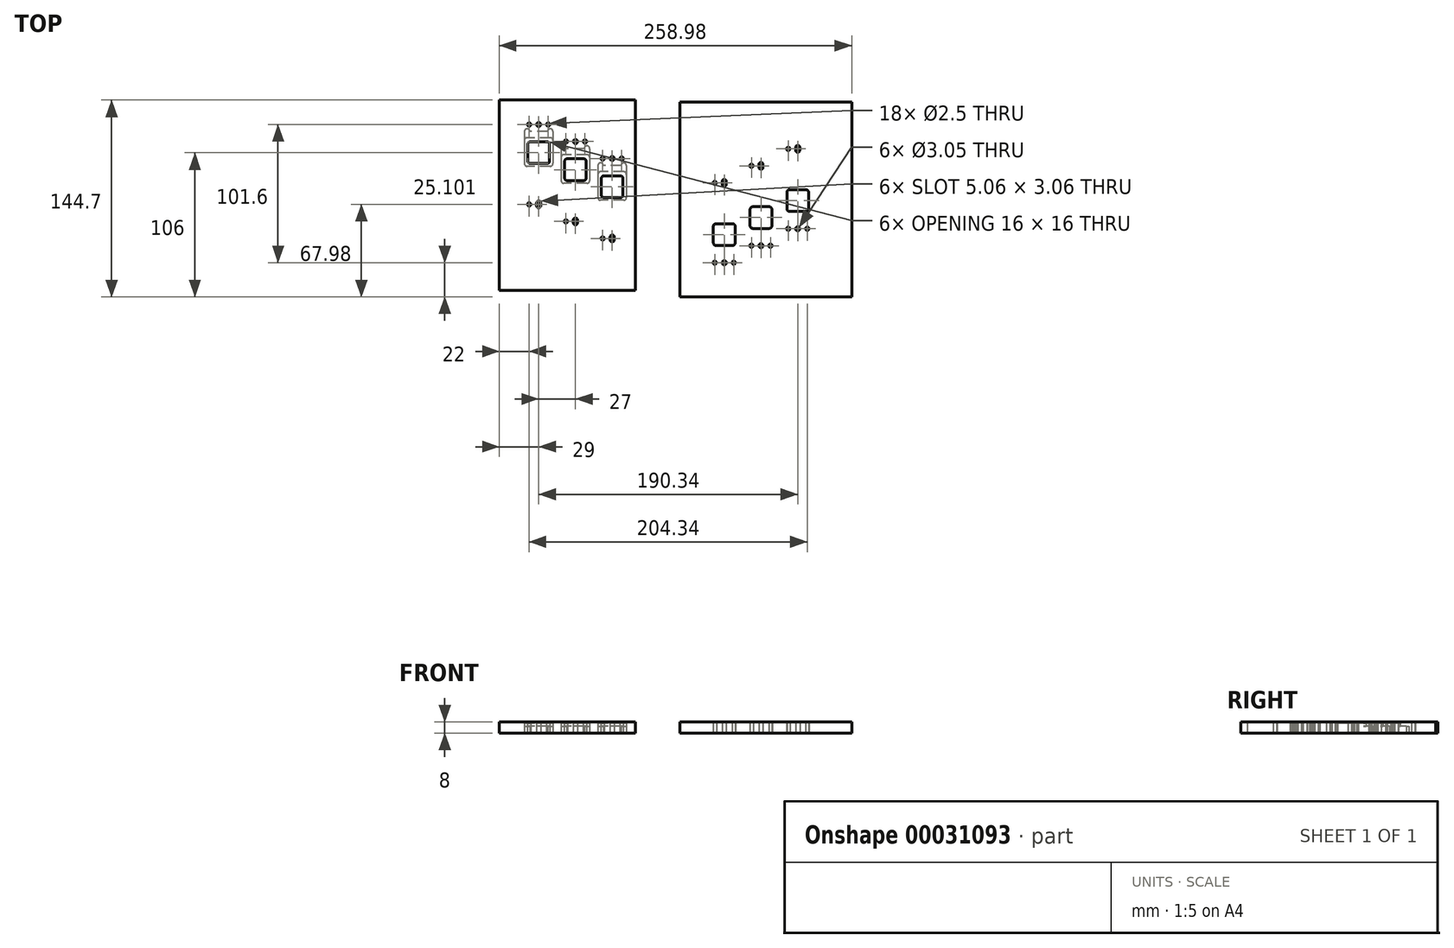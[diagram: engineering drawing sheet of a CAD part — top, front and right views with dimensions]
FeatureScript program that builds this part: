
annotation { "Feature Type Name" : "Feature", "Feature Type Description" : "" }
export const myFeature = defineFeature(function(context is Context, id is Id, definition is map)
    precondition{}
    {
        {
            var Q0;
            Q0=qCreatedBy(makeId("Top.planeOp"),FACE);
            var sketch = newSketch(context, id + "F0", { "sketchPlane" : qUnion([Q0])});
            skLineSegment(sketch, "E0.bottom", {"start": v(-50, 70) * mm, "end": v(50, 70) * mm});
            skLineSegment(sketch, "E0.top", {"start": v(-50, -70) * mm, "end": v(50, -70) * mm});
            skLineSegment(sketch, "E0.left", {"start": v(-50, 70) * mm, "end": v(-50, -70) * mm});
            skLineSegment(sketch, "E0.right", {"start": v(50, 70) * mm, "end": v(50, -70) * mm});
            skLineSegment(sketch, "E1", {"start": v(-50, -70) * mm, "end": v(50, 70) * mm, "construction": true});
            skSolve(sketch);
        }
        {
            var Q0;
            Q0=qSketchRegion(id+"F0",true);
            extrude(context, id + "F1", {"entities" : qUnion([Q0]), "depth" : 8 * mm});
        }
        {
            var Q0;
            Q0=makeQuery(id+"F1.opExtrude","CAP_FACE",FACE,{"disambiguationData":[OSD([sQuery(id+"F0.wireOp",EDGE,"E0.bottom"),sQuery(id+"F0.wireOp",EDGE,"E0.top"),sQuery(id+"F0.wireOp",EDGE,"E0.left"),sQuery(id+"F0.wireOp",EDGE,"E0.right")])],"isStart":true});
            var sketch = newSketch(context, id + "F2", { "sketchPlane" : qUnion([Q0])});
            skLineSegment(sketch, "E2", {"start": v(-21, -52) * mm, "end": v(-21, 6.72) * mm, "construction": true});
            skLineSegment(sketch, "E3", {"start": v(6, -39.5) * mm, "end": v(6, 19.22) * mm, "construction": true});
            skLineSegment(sketch, "E4", {"start": v(33, -27) * mm, "end": v(33, 31.72) * mm, "construction": true});
            skLineSegment(sketch, "E5", {"start": v(-14, -52) * mm, "end": v(-28, -52) * mm, "construction": true});
            skLineSegment(sketch, "E6", {"start": v(13, -39.5) * mm, "end": v(-1, -39.5) * mm, "construction": true});
            skLineSegment(sketch, "E7", {"start": v(40, -27) * mm, "end": v(26, -27) * mm, "construction": true});
            skLineSegment(sketch, "E8", {"start": v(-21, 6.72) * mm, "end": v(-28, 6.72) * mm, "construction": true});
            skLineSegment(sketch, "E9", {"start": v(6, 19.22) * mm, "end": v(-1, 19.22) * mm, "construction": true});
            skLineSegment(sketch, "E10", {"start": v(33, 31.72) * mm, "end": v(26, 31.72) * mm, "construction": true});
            skCircle(sketch, "E11", {"center": v(-28, -52) * mm, "radius": 1.25 * mm});
            skCircle(sketch, "E12", {"center": v(-14, -52) * mm, "radius": 1.25 * mm});
            skCircle(sketch, "E13", {"center": v(-28, 6.72) * mm, "radius": 1.25 * mm});
            skCircle(sketch, "E14", {"center": v(-1, -39.5) * mm, "radius": 1.25 * mm});
            skCircle(sketch, "E15", {"center": v(13, -39.5) * mm, "radius": 1.25 * mm});
            skCircle(sketch, "E16", {"center": v(-1, 19.22) * mm, "radius": 1.25 * mm});
            skCircle(sketch, "E17", {"center": v(26, 31.72) * mm, "radius": 1.25 * mm});
            skCircle(sketch, "E18", {"center": v(26, -27) * mm, "radius": 1.25 * mm});
            skCircle(sketch, "E19", {"center": v(40, -27) * mm, "radius": 1.25 * mm});
            skLineSegment(sketch, "E20", {"start": v(-21, 5.72) * mm, "end": v(-21, 7.72) * mm});
            skArc(sketch, "E21.0.startCap", {"start": v(-19.47, 5.72) * mm, "mid": v(-21, 4.2) * mm, "end": v(-22.53, 5.72) * mm});
            skArc(sketch, "E21.0.endCap", {"start": v(-22.53, 7.72) * mm, "mid": v(-21, 9.25) * mm, "end": v(-19.47, 7.72) * mm});
            skLineSegment(sketch, "E21.0.left", {"start": v(-22.53, 5.72) * mm, "end": v(-22.53, 7.72) * mm});
            skLineSegment(sketch, "E21.0.right", {"start": v(-19.47, 5.72) * mm, "end": v(-19.47, 7.72) * mm});
            skArc(sketch, "E22.0.startCap", {"start": v(7.53, 18.22) * mm, "mid": v(6, 16.7) * mm, "end": v(4.47, 18.22) * mm});
            skLineSegment(sketch, "E22.0.left", {"start": v(4.47, 18.22) * mm, "end": v(4.47, 20.22) * mm});
            skLineSegment(sketch, "E23", {"start": v(6, 18.22) * mm, "end": v(6, 20.22) * mm});
            skLineSegment(sketch, "E22.0.right", {"start": v(7.53, 18.22) * mm, "end": v(7.53, 20.22) * mm});
            skArc(sketch, "E22.0.endCap", {"start": v(4.47, 20.22) * mm, "mid": v(6, 21.75) * mm, "end": v(7.53, 20.22) * mm});
            skArc(sketch, "E24.0.startCap", {"start": v(34.53, 30.72) * mm, "mid": v(33, 29.2) * mm, "end": v(31.47, 30.72) * mm});
            skLineSegment(sketch, "E24.0.left", {"start": v(31.47, 30.72) * mm, "end": v(31.47, 32.72) * mm});
            skLineSegment(sketch, "E25", {"start": v(33, 30.72) * mm, "end": v(33, 32.72) * mm});
            skLineSegment(sketch, "E24.0.right", {"start": v(34.53, 30.72) * mm, "end": v(34.53, 32.72) * mm});
            skArc(sketch, "E24.0.endCap", {"start": v(31.47, 32.72) * mm, "mid": v(33, 34.25) * mm, "end": v(34.53, 32.72) * mm});
            skCircle(sketch, "E26", {"center": v(33, -27) * mm, "radius": 1.52 * mm});
            skCircle(sketch, "E27", {"center": v(6, -39.5) * mm, "radius": 1.52 * mm});
            skCircle(sketch, "E28", {"center": v(-21, -52) * mm, "radius": 1.52 * mm});
            skSolve(sketch);
        }
        {
            var Q0;
            Q0=qSketchRegion(id+"F2",true);
            var Q1;
            Q1=makeQuery(id+"F1.opExtrude","CAP_FACE",FACE,{"disambiguationData":[OSD([sQuery(id+"F0.wireOp",EDGE,"E0.bottom"),sQuery(id+"F0.wireOp",EDGE,"E0.top"),sQuery(id+"F0.wireOp",EDGE,"E0.left"),sQuery(id+"F0.wireOp",EDGE,"E0.right")])],"isStart":false});
            extrude(context, id + "F3", {"entities" : qUnion([Q0]), "operationType" : NewBodyOperationType.REMOVE, "endBound" : BoundingType.UP_TO_SURFACE, "oppositeDirection" : true, "endBoundEntityFace" : qUnion([Q1]), "depth" : 25 * mm});
        }
        {
            var Q0;
            Q0=makeQuery(id+"F1.opExtrude","CAP_FACE",FACE,{"disambiguationData":[OSD([sQuery(id+"F0.wireOp",EDGE,"E0.bottom"),sQuery(id+"F0.wireOp",EDGE,"E0.top"),sQuery(id+"F0.wireOp",EDGE,"E0.left"),sQuery(id+"F0.wireOp",EDGE,"E0.right")])],"isStart":true});
            var sketch = newSketch(context, id + "F4", { "sketchPlane" : qUnion([Q0])});
            skCircle(sketch, "E29", {"center": v(40, -27) * mm, "radius": 1.5 * mm});
            skCircle(sketch, "E30", {"center": v(26, -27) * mm, "radius": 1.5 * mm});
            skCircle(sketch, "E31", {"center": v(13, -39.5) * mm, "radius": 1.5 * mm});
            skCircle(sketch, "E32", {"center": v(-1, -39.5) * mm, "radius": 1.5 * mm});
            skCircle(sketch, "E33", {"center": v(-14, -52) * mm, "radius": 1.5 * mm});
            skCircle(sketch, "E34", {"center": v(-28, -52) * mm, "radius": 1.5 * mm});
            skCircle(sketch, "E35", {"center": v(-1, 19.22) * mm, "radius": 1.5 * mm});
            skCircle(sketch, "E36", {"center": v(-28, 6.72) * mm, "radius": 1.5 * mm});
            skCircle(sketch, "E37", {"center": v(26, 31.72) * mm, "radius": 1.5 * mm});
            skSolve(sketch);
        }
        {
            var Q0;
            Q0=makeQuery(id+"F4.imprint","IMPRINT",FACE,{"disambiguationData":[TD([[makeQuery(id+"F4.imprint","IMPRINT",EDGE,{"derivedFrom":sQuery(id+"F4.wireOp",EDGE,"E29")}),-1.0]])]});
            var sketch = newSketch(context, id + "F5", { "sketchPlane" : qUnion([Q0])});
            skLineSegment(sketch, "E38.bottom", {"start": v(39.5, -21.8) * mm, "end": v(26.5, -21.8) * mm});
            skLineSegment(sketch, "E38.top", {"start": v(41.5, 3.7) * mm, "end": v(24.5, 3.7) * mm});
            skLineSegment(sketch, "E38.left", {"start": v(43.5, -21.8) * mm, "end": v(43.5, 1.7) * mm});
            skLineSegment(sketch, "E38.right", {"start": v(22.5, -21.8) * mm, "end": v(22.5, 1.7) * mm});
            skLineSegment(sketch, "E39", {"start": v(33, -21.8) * mm, "end": v(33, -27) * mm, "construction": true});
            skArc(sketch, "E40", {"start": v(39.5, -21.8) * mm, "mid": v(41.5, -23.8) * mm, "end": v(43.5, -21.8) * mm});
            skArc(sketch, "E41", {"start": v(22.5, -21.8) * mm, "mid": v(24.5, -23.8) * mm, "end": v(26.5, -21.8) * mm});
            skPoint(sketch, "E42.visualSharp", {"position": v(43.5, 3.7) * mm});
            skArc(sketch, "E42.filletArc", {"start": v(43.5, 1.7) * mm, "mid": v(42.91, 3.11) * mm, "end": v(41.5, 3.7) * mm});
            skPoint(sketch, "E43.visualSharp", {"position": v(22.5, 3.7) * mm});
            skArc(sketch, "E43.filletArc", {"start": v(24.5, 3.7) * mm, "mid": v(23.09, 3.11) * mm, "end": v(22.5, 1.7) * mm});
            skLineSegment(sketch, "E44.top", {"start": v(14.5, -8.8) * mm, "end": v(-2.5, -8.8) * mm});
            skLineSegment(sketch, "E44.bottom", {"start": v(12.5, -34.3) * mm, "end": v(-0.5, -34.3) * mm});
            skLineSegment(sketch, "E44.right", {"start": v(-4.5, -34.3) * mm, "end": v(-4.5, -10.8) * mm});
            skArc(sketch, "E45", {"start": v(12.5, -34.3) * mm, "mid": v(14.5, -36.3) * mm, "end": v(16.5, -34.3) * mm});
            skLineSegment(sketch, "E44.left", {"start": v(16.5, -34.3) * mm, "end": v(16.5, -10.8) * mm});
            skArc(sketch, "E46", {"start": v(-4.5, -34.3) * mm, "mid": v(-2.5, -36.3) * mm, "end": v(-0.5, -34.3) * mm});
            skPoint(sketch, "E47.visualSharp", {"position": v(16.5, -8.8) * mm});
            skPoint(sketch, "E48.visualSharp", {"position": v(-4.5, -8.8) * mm});
            skLineSegment(sketch, "E49", {"start": v(6, -34.3) * mm, "end": v(6, -39.5) * mm, "construction": true});
            skArc(sketch, "E48.filletArc", {"start": v(-2.5, -8.8) * mm, "mid": v(-3.91, -9.39) * mm, "end": v(-4.5, -10.8) * mm});
            skArc(sketch, "E47.filletArc", {"start": v(16.5, -10.8) * mm, "mid": v(15.91, -9.39) * mm, "end": v(14.5, -8.8) * mm});
            skLineSegment(sketch, "E50.top", {"start": v(-12.5, -21.3) * mm, "end": v(-29.5, -21.3) * mm});
            skLineSegment(sketch, "E50.bottom", {"start": v(-14.5, -46.8) * mm, "end": v(-27.5, -46.8) * mm});
            skLineSegment(sketch, "E50.right", {"start": v(-31.5, -46.8) * mm, "end": v(-31.5, -23.3) * mm});
            skArc(sketch, "E51", {"start": v(-14.5, -46.8) * mm, "mid": v(-12.5, -48.8) * mm, "end": v(-10.5, -46.8) * mm});
            skLineSegment(sketch, "E50.left", {"start": v(-10.5, -46.8) * mm, "end": v(-10.5, -23.3) * mm});
            skArc(sketch, "E52", {"start": v(-31.5, -46.8) * mm, "mid": v(-29.5, -48.8) * mm, "end": v(-27.5, -46.8) * mm});
            skPoint(sketch, "E53.visualSharp", {"position": v(-10.5, -21.3) * mm});
            skPoint(sketch, "E54.visualSharp", {"position": v(-31.5, -21.3) * mm});
            skLineSegment(sketch, "E55", {"start": v(-21, -46.8) * mm, "end": v(-21, -52) * mm, "construction": true});
            skArc(sketch, "E54.filletArc", {"start": v(-29.5, -21.3) * mm, "mid": v(-30.91, -21.89) * mm, "end": v(-31.5, -23.3) * mm});
            skArc(sketch, "E53.filletArc", {"start": v(-10.5, -23.3) * mm, "mid": v(-11.09, -21.89) * mm, "end": v(-12.5, -21.3) * mm});
            skSolve(sketch);
        }
        {
            var Q0;
            Q0=qSketchRegion(id+"F5",true);
            extrude(context, id + "F6", {"entities" : qUnion([Q0]), "operationType" : NewBodyOperationType.REMOVE, "oppositeDirection" : true, "depth" : 5 * mm});
        }
        {
            var Q0;
            Q0=makeQuery(id+"F4.imprint","IMPRINT",FACE,{"disambiguationData":[TD([[makeQuery(id+"F4.imprint","IMPRINT",EDGE,{"derivedFrom":sQuery(id+"F4.wireOp",EDGE,"E29")}),-1.0]])]});
            var sketch = newSketch(context, id + "F7", { "sketchPlane" : qUnion([Q0])});
            skLineSegment(sketch, "E56.bottom", {"start": v(41.5, -17.3) * mm, "end": v(24.5, -17.3) * mm});
            skLineSegment(sketch, "E56.top", {"start": v(41.5, 3.7) * mm, "end": v(24.5, 3.7) * mm});
            skLineSegment(sketch, "E56.left", {"start": v(43.5, -15.3) * mm, "end": v(43.5, 1.7) * mm});
            skLineSegment(sketch, "E56.right", {"start": v(22.5, -15.3) * mm, "end": v(22.5, 1.7) * mm});
            skLineSegment(sketch, "E57", {"start": v(33, -17.3) * mm, "end": v(33, -27) * mm, "construction": true});
            skPoint(sketch, "E58.visualSharp", {"position": v(43.5, -17.3) * mm});
            skArc(sketch, "E58.filletArc", {"start": v(41.5, -17.3) * mm, "mid": v(42.91, -16.71) * mm, "end": v(43.5, -15.3) * mm});
            skPoint(sketch, "E59.visualSharp", {"position": v(43.5, 3.7) * mm});
            skArc(sketch, "E59.filletArc", {"start": v(43.5, 1.7) * mm, "mid": v(42.91, 3.11) * mm, "end": v(41.5, 3.7) * mm});
            skPoint(sketch, "E60.visualSharp", {"position": v(22.5, 3.7) * mm});
            skArc(sketch, "E60.filletArc", {"start": v(24.5, 3.7) * mm, "mid": v(23.09, 3.11) * mm, "end": v(22.5, 1.7) * mm});
            skPoint(sketch, "E61.visualSharp", {"position": v(22.5, -17.3) * mm});
            skArc(sketch, "E61.filletArc", {"start": v(22.5, -15.3) * mm, "mid": v(23.09, -16.71) * mm, "end": v(24.5, -17.3) * mm});
            skPoint(sketch, "E62.visualSharp", {"position": v(-4.5, -8.8) * mm});
            skLineSegment(sketch, "E63.left", {"start": v(16.5, -27.8) * mm, "end": v(16.5, -10.8) * mm});
            skPoint(sketch, "E64.visualSharp", {"position": v(-4.5, -29.8) * mm});
            skLineSegment(sketch, "E63.bottom", {"start": v(14.5, -29.8) * mm, "end": v(-2.5, -29.8) * mm});
            skPoint(sketch, "E65.visualSharp", {"position": v(16.5, -8.8) * mm});
            skLineSegment(sketch, "E63.right", {"start": v(-4.5, -27.8) * mm, "end": v(-4.5, -10.8) * mm});
            skPoint(sketch, "E66.visualSharp", {"position": v(16.5, -29.8) * mm});
            skLineSegment(sketch, "E63.top", {"start": v(14.5, -8.8) * mm, "end": v(-2.5, -8.8) * mm});
            skArc(sketch, "E65.filletArc", {"start": v(16.5, -10.8) * mm, "mid": v(15.91, -9.39) * mm, "end": v(14.5, -8.8) * mm});
            skArc(sketch, "E66.filletArc", {"start": v(14.5, -29.8) * mm, "mid": v(15.91, -29.21) * mm, "end": v(16.5, -27.8) * mm});
            skArc(sketch, "E62.filletArc", {"start": v(-2.5, -8.8) * mm, "mid": v(-3.91, -9.39) * mm, "end": v(-4.5, -10.8) * mm});
            skArc(sketch, "E64.filletArc", {"start": v(-4.5, -27.8) * mm, "mid": v(-3.91, -29.21) * mm, "end": v(-2.5, -29.8) * mm});
            skLineSegment(sketch, "E67", {"start": v(6, -29.8) * mm, "end": v(6, -39.5) * mm, "construction": true});
            skPoint(sketch, "E68.visualSharp", {"position": v(-31.5, -21.3) * mm});
            skLineSegment(sketch, "E69.left", {"start": v(-10.5, -40.3) * mm, "end": v(-10.5, -23.3) * mm});
            skPoint(sketch, "E70.visualSharp", {"position": v(-31.5, -42.3) * mm});
            skLineSegment(sketch, "E69.bottom", {"start": v(-12.5, -42.3) * mm, "end": v(-29.5, -42.3) * mm});
            skPoint(sketch, "E71.visualSharp", {"position": v(-10.5, -21.3) * mm});
            skLineSegment(sketch, "E69.right", {"start": v(-31.5, -40.3) * mm, "end": v(-31.5, -23.3) * mm});
            skPoint(sketch, "E72.visualSharp", {"position": v(-10.5, -42.3) * mm});
            skLineSegment(sketch, "E69.top", {"start": v(-12.5, -21.3) * mm, "end": v(-29.5, -21.3) * mm});
            skArc(sketch, "E71.filletArc", {"start": v(-10.5, -23.3) * mm, "mid": v(-11.09, -21.89) * mm, "end": v(-12.5, -21.3) * mm});
            skArc(sketch, "E72.filletArc", {"start": v(-12.5, -42.3) * mm, "mid": v(-11.09, -41.71) * mm, "end": v(-10.5, -40.3) * mm});
            skArc(sketch, "E68.filletArc", {"start": v(-29.5, -21.3) * mm, "mid": v(-30.91, -21.89) * mm, "end": v(-31.5, -23.3) * mm});
            skArc(sketch, "E70.filletArc", {"start": v(-31.5, -40.3) * mm, "mid": v(-30.91, -41.71) * mm, "end": v(-29.5, -42.3) * mm});
            skLineSegment(sketch, "E73", {"start": v(-21, -42.3) * mm, "end": v(-21, -52) * mm, "construction": true});
            skSolve(sketch);
        }
        {
            var Q0;
            Q0=qSketchRegion(id+"F7",true);
            extrude(context, id + "F8", {"entities" : qUnion([Q0]), "operationType" : NewBodyOperationType.REMOVE, "oppositeDirection" : true, "depth" : 7 * mm});
        }
        {
            var Q0;
            Q0=makeQuery(id+"F4.imprint","IMPRINT",FACE,{"disambiguationData":[TD([[makeQuery(id+"F4.imprint","IMPRINT",EDGE,{"derivedFrom":sQuery(id+"F4.wireOp",EDGE,"E29")}),-1.0]])]});
            var sketch = newSketch(context, id + "F9", { "sketchPlane" : qUnion([Q0])});
            skLineSegment(sketch, "E74.bottom", {"start": v(39, -14.3) * mm, "end": v(27, -14.3) * mm});
            skLineSegment(sketch, "E74.top", {"start": v(39, 1.7) * mm, "end": v(27, 1.7) * mm});
            skLineSegment(sketch, "E74.left", {"start": v(41, -12.3) * mm, "end": v(41, -0.3) * mm});
            skLineSegment(sketch, "E74.right", {"start": v(25, -12.3) * mm, "end": v(25, -0.3) * mm});
            skLineSegment(sketch, "E75", {"start": v(33, -14.3) * mm, "end": v(33, -27) * mm, "construction": true});
            skLineSegment(sketch, "E76", {"start": v(6, -26.8) * mm, "end": v(6, -39.5) * mm, "construction": true});
            skLineSegment(sketch, "E77.right", {"start": v(-2, -24.8) * mm, "end": v(-2, -12.8) * mm});
            skLineSegment(sketch, "E77.left", {"start": v(14, -24.8) * mm, "end": v(14, -12.8) * mm});
            skLineSegment(sketch, "E77.top", {"start": v(12, -10.8) * mm, "end": v(0, -10.8) * mm});
            skLineSegment(sketch, "E77.bottom", {"start": v(12, -26.8) * mm, "end": v(0, -26.8) * mm});
            skLineSegment(sketch, "E78", {"start": v(-21, -39.3) * mm, "end": v(-21, -52) * mm, "construction": true});
            skLineSegment(sketch, "E79.right", {"start": v(-29, -37.3) * mm, "end": v(-29, -25.3) * mm});
            skLineSegment(sketch, "E79.left", {"start": v(-13, -37.3) * mm, "end": v(-13, -25.3) * mm});
            skLineSegment(sketch, "E79.top", {"start": v(-15, -23.3) * mm, "end": v(-27, -23.3) * mm});
            skLineSegment(sketch, "E79.bottom", {"start": v(-15, -39.3) * mm, "end": v(-27, -39.3) * mm});
            skPoint(sketch, "E80.visualSharp", {"position": v(41, -14.3) * mm});
            skArc(sketch, "E80.filletArc", {"start": v(39, -14.3) * mm, "mid": v(40.41, -13.71) * mm, "end": v(41, -12.3) * mm});
            skPoint(sketch, "E81.visualSharp", {"position": v(41, 1.7) * mm});
            skArc(sketch, "E81.filletArc", {"start": v(41, -0.3) * mm, "mid": v(40.41, 1.11) * mm, "end": v(39, 1.7) * mm});
            skPoint(sketch, "E82.visualSharp", {"position": v(25, 1.7) * mm});
            skArc(sketch, "E82.filletArc", {"start": v(27, 1.7) * mm, "mid": v(25.59, 1.11) * mm, "end": v(25, -0.3) * mm});
            skPoint(sketch, "E83.visualSharp", {"position": v(25, -14.3) * mm});
            skArc(sketch, "E83.filletArc", {"start": v(25, -12.3) * mm, "mid": v(25.59, -13.71) * mm, "end": v(27, -14.3) * mm});
            skPoint(sketch, "E84.visualSharp", {"position": v(14, -26.8) * mm});
            skArc(sketch, "E84.filletArc", {"start": v(12, -26.8) * mm, "mid": v(13.41, -26.21) * mm, "end": v(14, -24.8) * mm});
            skPoint(sketch, "E85.visualSharp", {"position": v(14, -10.8) * mm});
            skArc(sketch, "E85.filletArc", {"start": v(14, -12.8) * mm, "mid": v(13.41, -11.39) * mm, "end": v(12, -10.8) * mm});
            skPoint(sketch, "E86.visualSharp", {"position": v(-2, -10.8) * mm});
            skArc(sketch, "E86.filletArc", {"start": v(0, -10.8) * mm, "mid": v(-1.41, -11.39) * mm, "end": v(-2, -12.8) * mm});
            skPoint(sketch, "E87.visualSharp", {"position": v(-2, -26.8) * mm});
            skArc(sketch, "E87.filletArc", {"start": v(-2, -24.8) * mm, "mid": v(-1.41, -26.21) * mm, "end": v(0, -26.8) * mm});
            skPoint(sketch, "E88.visualSharp", {"position": v(-13, -39.3) * mm});
            skArc(sketch, "E88.filletArc", {"start": v(-15, -39.3) * mm, "mid": v(-13.59, -38.71) * mm, "end": v(-13, -37.3) * mm});
            skPoint(sketch, "E89.visualSharp", {"position": v(-13, -23.3) * mm});
            skArc(sketch, "E89.filletArc", {"start": v(-13, -25.3) * mm, "mid": v(-13.59, -23.89) * mm, "end": v(-15, -23.3) * mm});
            skPoint(sketch, "E90.visualSharp", {"position": v(-29, -23.3) * mm});
            skArc(sketch, "E90.filletArc", {"start": v(-27, -23.3) * mm, "mid": v(-28.41, -23.89) * mm, "end": v(-29, -25.3) * mm});
            skPoint(sketch, "E91.visualSharp", {"position": v(-29, -39.3) * mm});
            skArc(sketch, "E91.filletArc", {"start": v(-29, -37.3) * mm, "mid": v(-28.41, -38.71) * mm, "end": v(-27, -39.3) * mm});
            skSolve(sketch);
        }
        {
            var Q0;
            Q0=qSketchRegion(id+"F9",true);
            var Q1;
            Q1=makeQuery(id+"F1.opExtrude","CAP_FACE",FACE,{"disambiguationData":[OSD([sQuery(id+"F0.wireOp",EDGE,"E0.bottom"),sQuery(id+"F0.wireOp",EDGE,"E0.top"),sQuery(id+"F0.wireOp",EDGE,"E0.left"),sQuery(id+"F0.wireOp",EDGE,"E0.right")])],"isStart":false});
            extrude(context, id + "F10", {"entities" : qUnion([Q0]), "operationType" : NewBodyOperationType.REMOVE, "endBound" : BoundingType.UP_TO_SURFACE, "oppositeDirection" : true, "endBoundEntityFace" : qUnion([Q1]), "depth" : 25 * mm});
        }
        {
            var Q0;
            Q0=qCreatedBy(makeId("Top.planeOp"),FACE);
            var sketch = newSketch(context, id + "F11", { "sketchPlane" : qUnion([Q0])});
            skLineSegment(sketch, "E92.bottom", {"start": v(82.68, 68.5) * mm, "end": v(208.98, 68.5) * mm});
            skLineSegment(sketch, "E92.top", {"start": v(82.68, -74.7) * mm, "end": v(208.98, -74.7) * mm});
            skLineSegment(sketch, "E92.left", {"start": v(82.68, 68.5) * mm, "end": v(82.68, -74.7) * mm});
            skLineSegment(sketch, "E92.right", {"start": v(208.98, 68.5) * mm, "end": v(208.98, -74.7) * mm});
            skLineSegment(sketch, "E93", {"start": v(115.34, -49.6) * mm, "end": v(115.34, 9.12) * mm, "construction": true});
            skLineSegment(sketch, "E94", {"start": v(142.34, -37.1) * mm, "end": v(142.34, 21.62) * mm, "construction": true});
            skLineSegment(sketch, "E95", {"start": v(169.34, -24.6) * mm, "end": v(169.34, 34.12) * mm, "construction": true});
            skLineSegment(sketch, "E96", {"start": v(122.34, -49.6) * mm, "end": v(108.34, -49.6) * mm, "construction": true});
            skLineSegment(sketch, "E97", {"start": v(149.34, -37.1) * mm, "end": v(135.34, -37.1) * mm, "construction": true});
            skLineSegment(sketch, "E98", {"start": v(176.34, -24.6) * mm, "end": v(162.34, -24.6) * mm, "construction": true});
            skLineSegment(sketch, "E99", {"start": v(115.34, 9.12) * mm, "end": v(108.34, 9.12) * mm, "construction": true});
            skLineSegment(sketch, "E100", {"start": v(142.34, 21.62) * mm, "end": v(135.34, 21.62) * mm, "construction": true});
            skLineSegment(sketch, "E101", {"start": v(169.34, 34.12) * mm, "end": v(162.34, 34.12) * mm, "construction": true});
            skCircle(sketch, "E102", {"center": v(108.34, -49.6) * mm, "radius": 1.25 * mm});
            skCircle(sketch, "E103", {"center": v(122.34, -49.6) * mm, "radius": 1.25 * mm});
            skCircle(sketch, "E104", {"center": v(108.34, 9.12) * mm, "radius": 1.25 * mm});
            skCircle(sketch, "E105", {"center": v(135.34, -37.1) * mm, "radius": 1.25 * mm});
            skCircle(sketch, "E106", {"center": v(149.34, -37.1) * mm, "radius": 1.25 * mm});
            skCircle(sketch, "E107", {"center": v(135.34, 21.62) * mm, "radius": 1.25 * mm});
            skCircle(sketch, "E108", {"center": v(162.34, 34.12) * mm, "radius": 1.25 * mm});
            skCircle(sketch, "E109", {"center": v(162.34, -24.6) * mm, "radius": 1.25 * mm});
            skCircle(sketch, "E110", {"center": v(176.34, -24.6) * mm, "radius": 1.25 * mm});
            skLineSegment(sketch, "E111", {"start": v(115.34, 8.12) * mm, "end": v(115.34, 10.12) * mm});
            skArc(sketch, "E112.0.startCap", {"start": v(116.87, 8.12) * mm, "mid": v(115.34, 6.6) * mm, "end": v(113.81, 8.12) * mm});
            skArc(sketch, "E112.0.endCap", {"start": v(113.81, 10.12) * mm, "mid": v(115.34, 11.65) * mm, "end": v(116.87, 10.12) * mm});
            skLineSegment(sketch, "E112.0.left", {"start": v(113.81, 8.12) * mm, "end": v(113.81, 10.12) * mm});
            skLineSegment(sketch, "E112.0.right", {"start": v(116.87, 8.12) * mm, "end": v(116.87, 10.12) * mm});
            skArc(sketch, "E113.0.startCap", {"start": v(143.87, 20.62) * mm, "mid": v(142.34, 19.1) * mm, "end": v(140.81, 20.62) * mm});
            skLineSegment(sketch, "E113.0.left", {"start": v(140.81, 20.62) * mm, "end": v(140.81, 22.62) * mm});
            skLineSegment(sketch, "E114", {"start": v(142.34, 20.62) * mm, "end": v(142.34, 22.62) * mm});
            skLineSegment(sketch, "E113.0.right", {"start": v(143.87, 20.62) * mm, "end": v(143.87, 22.62) * mm});
            skArc(sketch, "E113.0.endCap", {"start": v(140.81, 22.62) * mm, "mid": v(142.34, 24.15) * mm, "end": v(143.87, 22.62) * mm});
            skArc(sketch, "E115.0.startCap", {"start": v(170.87, 33.12) * mm, "mid": v(169.34, 31.6) * mm, "end": v(167.81, 33.12) * mm});
            skLineSegment(sketch, "E115.0.left", {"start": v(167.81, 33.12) * mm, "end": v(167.81, 35.12) * mm});
            skLineSegment(sketch, "E116", {"start": v(169.34, 33.12) * mm, "end": v(169.34, 35.12) * mm});
            skLineSegment(sketch, "E115.0.right", {"start": v(170.87, 33.12) * mm, "end": v(170.87, 35.12) * mm});
            skArc(sketch, "E115.0.endCap", {"start": v(167.81, 35.12) * mm, "mid": v(169.34, 36.65) * mm, "end": v(170.87, 35.12) * mm});
            skCircle(sketch, "E117", {"center": v(169.34, -24.6) * mm, "radius": 1.52 * mm});
            skCircle(sketch, "E118", {"center": v(142.34, -37.1) * mm, "radius": 1.52 * mm});
            skCircle(sketch, "E119", {"center": v(115.34, -49.6) * mm, "radius": 1.52 * mm});
            skPoint(sketch, "E120.visualSharp", {"position": v(134.34, -8.4) * mm});
            skLineSegment(sketch, "E121.bottom", {"start": v(121.34, -36.9) * mm, "end": v(109.34, -36.9) * mm});
            skPoint(sketch, "E122.visualSharp", {"position": v(161.34, 4.1) * mm});
            skPoint(sketch, "E123.visualSharp", {"position": v(177.34, -11.9) * mm});
            skLineSegment(sketch, "E121.left", {"start": v(123.34, -34.9) * mm, "end": v(123.34, -22.9) * mm});
            skLineSegment(sketch, "E124.right", {"start": v(161.34, -9.9) * mm, "end": v(161.34, 2.1) * mm});
            skLineSegment(sketch, "E124.top", {"start": v(175.34, 4.1) * mm, "end": v(163.34, 4.1) * mm});
            skPoint(sketch, "E125.visualSharp", {"position": v(161.34, -11.9) * mm});
            skPoint(sketch, "E126.visualSharp", {"position": v(107.34, -20.9) * mm});
            skPoint(sketch, "E127.visualSharp", {"position": v(107.34, -36.9) * mm});
            skLineSegment(sketch, "E128.left", {"start": v(150.34, -22.4) * mm, "end": v(150.34, -10.4) * mm});
            skLineSegment(sketch, "E121.top", {"start": v(121.34, -20.9) * mm, "end": v(109.34, -20.9) * mm});
            skPoint(sketch, "E129.visualSharp", {"position": v(134.34, -24.4) * mm});
            skLineSegment(sketch, "E130", {"start": v(169.34, -11.9) * mm, "end": v(169.34, -24.6) * mm, "construction": true});
            skLineSegment(sketch, "E128.right", {"start": v(134.34, -22.4) * mm, "end": v(134.34, -10.4) * mm});
            skLineSegment(sketch, "E128.top", {"start": v(148.34, -8.4) * mm, "end": v(136.34, -8.4) * mm});
            skLineSegment(sketch, "E131", {"start": v(142.34, -24.4) * mm, "end": v(142.34, -37.1) * mm, "construction": true});
            skLineSegment(sketch, "E132", {"start": v(115.34, -36.9) * mm, "end": v(115.34, -49.6) * mm, "construction": true});
            skLineSegment(sketch, "E121.right", {"start": v(107.34, -34.9) * mm, "end": v(107.34, -22.9) * mm});
            skPoint(sketch, "E133.visualSharp", {"position": v(123.34, -36.9) * mm});
            skLineSegment(sketch, "E124.bottom", {"start": v(175.34, -11.9) * mm, "end": v(163.34, -11.9) * mm});
            skPoint(sketch, "E134.visualSharp", {"position": v(150.34, -8.4) * mm});
            skLineSegment(sketch, "E128.bottom", {"start": v(148.34, -24.4) * mm, "end": v(136.34, -24.4) * mm});
            skPoint(sketch, "E135.visualSharp", {"position": v(177.34, 4.1) * mm});
            skPoint(sketch, "E136.visualSharp", {"position": v(123.34, -20.9) * mm});
            skPoint(sketch, "E137.visualSharp", {"position": v(150.34, -24.4) * mm});
            skLineSegment(sketch, "E124.left", {"start": v(177.34, -9.9) * mm, "end": v(177.34, 2.1) * mm});
            skArc(sketch, "E135.filletArc", {"start": v(177.34, 2.1) * mm, "mid": v(176.75, 3.51) * mm, "end": v(175.34, 4.1) * mm});
            skArc(sketch, "E137.filletArc", {"start": v(148.34, -24.4) * mm, "mid": v(149.75, -23.81) * mm, "end": v(150.34, -22.4) * mm});
            skArc(sketch, "E125.filletArc", {"start": v(161.34, -9.9) * mm, "mid": v(161.93, -11.31) * mm, "end": v(163.34, -11.9) * mm});
            skArc(sketch, "E127.filletArc", {"start": v(107.34, -34.9) * mm, "mid": v(107.93, -36.31) * mm, "end": v(109.34, -36.9) * mm});
            skArc(sketch, "E126.filletArc", {"start": v(109.34, -20.9) * mm, "mid": v(107.93, -21.49) * mm, "end": v(107.34, -22.9) * mm});
            skArc(sketch, "E122.filletArc", {"start": v(163.34, 4.1) * mm, "mid": v(161.93, 3.51) * mm, "end": v(161.34, 2.1) * mm});
            skArc(sketch, "E134.filletArc", {"start": v(150.34, -10.4) * mm, "mid": v(149.75, -8.99) * mm, "end": v(148.34, -8.4) * mm});
            skArc(sketch, "E129.filletArc", {"start": v(134.34, -22.4) * mm, "mid": v(134.93, -23.81) * mm, "end": v(136.34, -24.4) * mm});
            skArc(sketch, "E133.filletArc", {"start": v(121.34, -36.9) * mm, "mid": v(122.75, -36.31) * mm, "end": v(123.34, -34.9) * mm});
            skArc(sketch, "E136.filletArc", {"start": v(123.34, -22.9) * mm, "mid": v(122.75, -21.49) * mm, "end": v(121.34, -20.9) * mm});
            skArc(sketch, "E120.filletArc", {"start": v(136.34, -8.4) * mm, "mid": v(134.93, -8.99) * mm, "end": v(134.34, -10.4) * mm});
            skArc(sketch, "E123.filletArc", {"start": v(175.34, -11.9) * mm, "mid": v(176.75, -11.31) * mm, "end": v(177.34, -9.9) * mm});
            skSolve(sketch);
        }
        {
            var Q0;
            Q0 = qSketchRegion(id + "F11", true);
            extrude(context, id + "F12", {"entities" : qUnion([Q0]), "depth" : 8 * mm});
        }
    });
